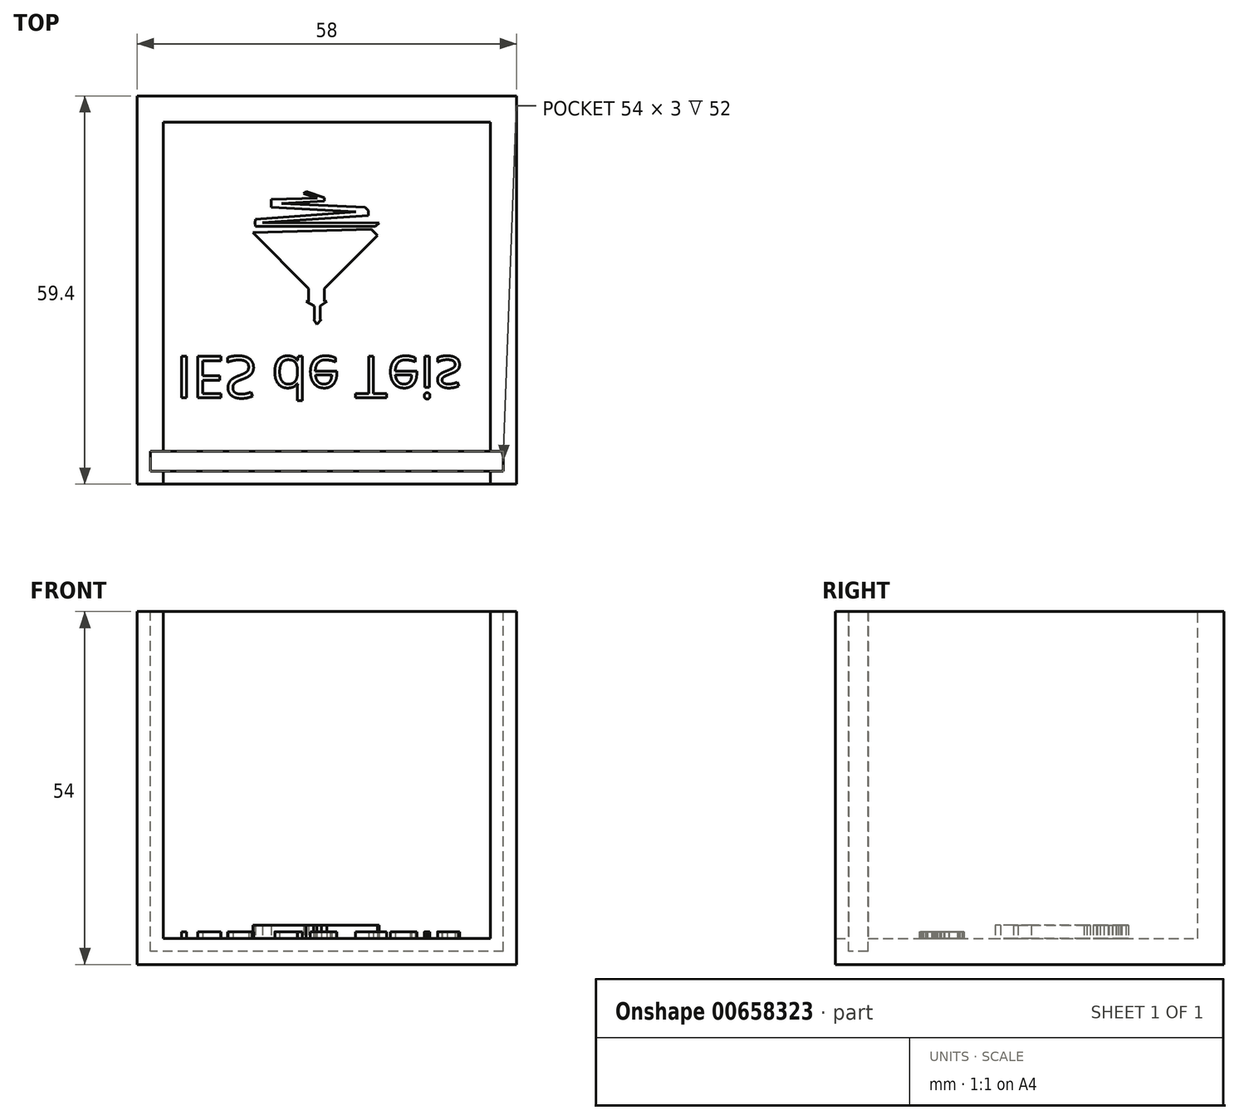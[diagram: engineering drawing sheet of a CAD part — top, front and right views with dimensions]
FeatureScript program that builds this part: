
annotation { "Feature Type Name" : "Feature", "Feature Type Description" : "" }
export const myFeature = defineFeature(function(context is Context, id is Id, definition is map)
    precondition{}
    {
        {
            var Q0;
            Q0=qCreatedBy(makeId("Front.planeOp"),FACE);
            var sketch = newSketch(context, id + "F0", { "sketchPlane" : qUnion([Q0])});
            skLineSegment(sketch, "E0.bottom", {"start": v(0, 0) * mm, "end": v(58, 0) * mm});
            skLineSegment(sketch, "E0.top", {"start": v(0, 54) * mm, "end": v(4, 54) * mm});
            skLineSegment(sketch, "E0.left", {"start": v(0, 0) * mm, "end": v(0, 54) * mm});
            skLineSegment(sketch, "E0.right", {"start": v(58, 0) * mm, "end": v(58, 54) * mm});
            skLineSegment(sketch, "E1", {"start": v(54, 54) * mm, "end": v(54, 4) * mm});
            skLineSegment(sketch, "E2", {"start": v(54, 4) * mm, "end": v(4, 4) * mm});
            skLineSegment(sketch, "E3", {"start": v(4, 4) * mm, "end": v(4, 54) * mm});
            skLineSegment(sketch, "E4.trimOffspring", {"start": v(54, 54) * mm, "end": v(58, 54) * mm});
            skSolve(sketch);
        }
        {
            var Q0;
            Q0=makeQuery(id+"F0.imprint","IMPRINT",FACE,{"disambiguationData":[TD([[makeQuery(id+"F0.imprint","IMPRINT",EDGE,{"derivedFrom":sQuery(id+"F0.wireOp",EDGE,"E0.bottom")}),1.0]])]});
            extrude(context, id + "F1", {"entities" : qUnion([Q0]), "depth" : 59.4 * mm, "offsetDistance" : 25 * mm});
        }
        {
            var Q0;
            Q0=makeQuery(id+"F0.imprint","IMPRINT",FACE,{"disambiguationData":[TD([[makeQuery(id+"F0.imprint","IMPRINT",EDGE,{"derivedFrom":sQuery(id+"F0.wireOp",EDGE,"E0.bottom")}),1.0]])]});
            var sketch = newSketch(context, id + "F2", { "sketchPlane" : qUnion([Q0])});
            skLineSegment(sketch, "E5", {"start": v(58, 54) * mm, "end": v(58, 0) * mm});
            skLineSegment(sketch, "E6", {"start": v(58, 0) * mm, "end": v(0, 0) * mm});
            skLineSegment(sketch, "E7", {"start": v(0, 0) * mm, "end": v(0, 54) * mm});
            skLineSegment(sketch, "E8", {"start": v(0, 54) * mm, "end": v(58, 54) * mm});
            skSolve(sketch);
        }
        {
            var Q0;
            Q0 = qSketchRegion(id + "F2", true);
            extrude(context, id + "F3", {"entities" : qUnion([Q0]), "operationType" : NewBodyOperationType.ADD, "depth" : 4 * mm, "offsetDistance" : 25 * mm});
        }
        {
            var Q0;
            Q0=makeQuery(id+"F3.boolean.opBoolean","MERGE",FACE,{"derivedFrom":[makeQuery(id+"F1.opExtrude","SWEPT_FACE",FACE,{"disambiguationData":[OSD([sQuery(id+"F0.wireOp",EDGE,"E0.top")])]}),makeQuery(id+"F1.opExtrude","SWEPT_FACE",FACE,{"disambiguationData":[OSD([sQuery(id+"F0.wireOp",EDGE,"E4.trimOffspring")])]}),makeQuery(id+"F3.opExtrude","SWEPT_FACE",FACE,{"disambiguationData":[OSD([sQuery(id+"F2.wireOp",EDGE,"E8")])]})]});
            var sketch = newSketch(context, id + "F4", { "sketchPlane" : qUnion([Q0])});
            skPoint(sketch, "E9", {"position": v(4, -57.4) * mm});
            skPoint(sketch, "E10", {"position": v(54, -57.4) * mm});
            skLineSegment(sketch, "E11", {"start": v(2, -54.4) * mm, "end": v(2, -57.4) * mm});
            skLineSegment(sketch, "E12", {"start": v(56, -54.4) * mm, "end": v(56, -57.4) * mm});
            skLineSegment(sketch, "E13", {"start": v(56, -54.4) * mm, "end": v(2, -54.4) * mm});
            skLineSegment(sketch, "E14", {"start": v(56, -57.4) * mm, "end": v(2, -57.4) * mm});
            skSolve(sketch);
        }
        {
            var Q0;
            {var subQ0=sQuery(id+"F4.wireOp",EDGE,"E11");Q0=makeQuery(id+"F4.imprint","IMPRINT",FACE,{"disambiguationData":[TD([[makeQuery(id+"F4.imprint","IMPRINT",EDGE,{"derivedFrom":subQ0}),1.0]])]});}
            var Q1;
            {var subQ0=sQuery(id+"F4.wireOp",EDGE,"E13");var subQ1=makeQuery(id+"F1.opExtrude","SWEPT_EDGE",EDGE,{"disambiguationData":[OSD([sQuery(id+"F0.wireOp",EDGE,"E1"),sQuery(id+"F0.wireOp",EDGE,"E4.trimOffspring")])]});var subQ2=makeQuery(id+"F4.imprint","INTERSECT",VERTEX,{"derivedFrom":[subQ1,subQ0]});Q1=makeQuery(id+"F4.imprint","IMPRINT",FACE,{"disambiguationData":[TD([[makeQuery(id+"F4.imprint","IMPRINT",EDGE,{"disambiguationData":[TD([[subQ2,-1.0]])],"derivedFrom":subQ0}),1.0]])]});}
            var Q2;
            {var subQ0=sQuery(id+"F4.wireOp",EDGE,"E12");Q2=makeQuery(id+"F4.imprint","IMPRINT",FACE,{"disambiguationData":[TD([[makeQuery(id+"F4.imprint","IMPRINT",EDGE,{"derivedFrom":subQ0}),-1.0]])]});}
            extrude(context, id + "F5", {"entities" : qUnion([Q0, Q1, Q2]), "operationType" : NewBodyOperationType.REMOVE, "oppositeDirection" : true, "depth" : 52 * mm, "offsetDistance" : 25 * mm});
        }
        {
            var Q0;
            Q0=makeQuery(id+"F1.opExtrude","SWEPT_FACE",FACE,{"disambiguationData":[OSD([sQuery(id+"F0.wireOp",EDGE,"E0.bottom")])]});
            var Q1;
            Q1 = qBodyType(qCreatedBy(id + "F7" ,EDGE), BodyType.WIRE);
            cPlane(context, id + "F6", {"entities" : qUnion([Q0, Q1]), "cplaneType" : CPlaneType.OFFSET, "offset" : 2 * mm, "oppositeDirection" : true, "width" : 150 * mm, "height" : 150 * mm});
        }
        {
            var Q0;
            Q0=qCreatedBy(id+"F6.planeOp",FACE);
            var sketch = newSketch(context, id + "F7", { "sketchPlane" : qUnion([Q0])});
            skText(sketch, "E15", { "text": "IES de Teis", "fontName": "OpenSans-Regular.ttf"});
            const initialGuessF7  = {"E15": [0.0059, 0.03985, 1, 0, 0.00641]};
            skSetInitialGuess(sketch, initialGuessF7);
            skSolve(sketch);
        }
        {
            var Q0;
            Q0 = qSketchRegion(id + "F7", true);
            extrude(context, id + "F8", {"entities" : qUnion([Q0]), "operationType" : NewBodyOperationType.ADD, "oppositeDirection" : true, "depth" : 3 * mm, "offsetDistance" : 25 * mm});
        }
        {
            var Q0;
            Q0=qCreatedBy(id+"F6.planeOp",FACE);
            var sketch = newSketch(context, id + "F9", { "sketchPlane" : qUnion([Q0])});
            skLineSegment(sketch, "E16", {"start": v(27.5, 34.96) * mm, "end": v(26.99, 34.16) * mm});
            skLineSegment(sketch, "E17", {"start": v(26.99, 34.16) * mm, "end": v(28.18, 34.16) * mm});
            skLineSegment(sketch, "E18", {"start": v(28.18, 34.16) * mm, "end": v(27.5, 34.96) * mm});
            skLineSegment(sketch, "E19", {"start": v(27.97, 34.16) * mm, "end": v(27.97, 32.17) * mm});
            skLineSegment(sketch, "E20", {"start": v(27.97, 32.17) * mm, "end": v(27.07, 32.17) * mm});
            skLineSegment(sketch, "E21", {"start": v(27.07, 32.17) * mm, "end": v(27.07, 34.16) * mm});
            skLineSegment(sketch, "E22", {"start": v(27.97, 32.17) * mm, "end": v(29, 31.47) * mm});
            skLineSegment(sketch, "E23", {"start": v(29, 31.47) * mm, "end": v(28.61, 31.47) * mm});
            skLineSegment(sketch, "E24", {"start": v(28.61, 31.47) * mm, "end": v(28.61, 29.48) * mm});
            skLineSegment(sketch, "E25", {"start": v(28.61, 29.48) * mm, "end": v(26.23, 29.48) * mm});
            skLineSegment(sketch, "E26", {"start": v(26.23, 29.48) * mm, "end": v(26.23, 31.45) * mm});
            skLineSegment(sketch, "E27", {"start": v(26.23, 31.45) * mm, "end": v(25.84, 31.45) * mm});
            skLineSegment(sketch, "E28", {"start": v(25.84, 31.45) * mm, "end": v(27.07, 32.17) * mm});
            skLineSegment(sketch, "E29", {"start": v(26.23, 29.48) * mm, "end": v(17.7, 20.92) * mm});
            skLineSegment(sketch, "E30", {"start": v(17.7, 20.92) * mm, "end": v(35.82, 20.41) * mm});
            skLineSegment(sketch, "E31", {"start": v(35.82, 20.41) * mm, "end": v(36.76, 21.35) * mm});
            skLineSegment(sketch, "E32", {"start": v(36.76, 21.35) * mm, "end": v(28.61, 29.48) * mm});
            skLineSegment(sketch, "E33", {"start": v(18.06, 19.99) * mm, "end": v(36.45, 19.99) * mm});
            skLineSegment(sketch, "E34", {"start": v(36.45, 19.99) * mm, "end": v(36.98, 19.46) * mm});
            skLineSegment(sketch, "E35", {"start": v(18.02, 19.45) * mm, "end": v(18.06, 19.99) * mm});
            skLineSegment(sketch, "E36", {"start": v(19.18, 19.37) * mm, "end": v(35.36, 18.3) * mm});
            skLineSegment(sketch, "E37", {"start": v(35.36, 18.3) * mm, "end": v(35.34, 17.56) * mm});
            skLineSegment(sketch, "E38", {"start": v(33.42, 17.7) * mm, "end": v(18.06, 18.9) * mm});
            skLineSegment(sketch, "E39", {"start": v(18.06, 18.9) * mm, "end": v(18.02, 19.45) * mm});
            skLineSegment(sketch, "E40", {"start": v(35.34, 17.56) * mm, "end": v(34.85, 17.07) * mm});
            skLineSegment(sketch, "E41", {"start": v(20.48, 16.51) * mm, "end": v(20.46, 17.02) * mm});
            skLineSegment(sketch, "E42", {"start": v(20.48, 16.51) * mm, "end": v(20.46, 15.81) * mm});
            skLineSegment(sketch, "E43", {"start": v(20.46, 15.81) * mm, "end": v(27.55, 15.61) * mm});
            skLineSegment(sketch, "E44", {"start": v(28.61, 15.58) * mm, "end": v(28.6, 16.11) * mm});
            skLineSegment(sketch, "E45", {"start": v(28.6, 16.11) * mm, "end": v(22.07, 16.43) * mm});
            skLineSegment(sketch, "E46", {"start": v(28.61, 15.58) * mm, "end": v(25.83, 14.6) * mm});
            skLineSegment(sketch, "E47", {"start": v(25.83, 14.6) * mm, "end": v(25.46, 14.97) * mm});
            skLineSegment(sketch, "E48", {"start": v(25.46, 14.97) * mm, "end": v(27.55, 15.61) * mm});
            skLineSegment(sketch, "E49", {"start": v(33.42, 17.7) * mm, "end": v(20.46, 17.02) * mm});
            skLineSegment(sketch, "E50", {"start": v(34.85, 17.07) * mm, "end": v(22.07, 16.43) * mm});
            skLineSegment(sketch, "E51", {"start": v(36.98, 19.46) * mm, "end": v(19.18, 19.37) * mm});
            skSolve(sketch);
        }
        {
            var Q0;
            Q0 = qSketchRegion(id + "F9", true);
            extrude(context, id + "F10", {"entities" : qUnion([Q0]), "operationType" : NewBodyOperationType.ADD, "oppositeDirection" : true, "depth" : 4 * mm, "offsetDistance" : 25 * mm});
        }
    });
